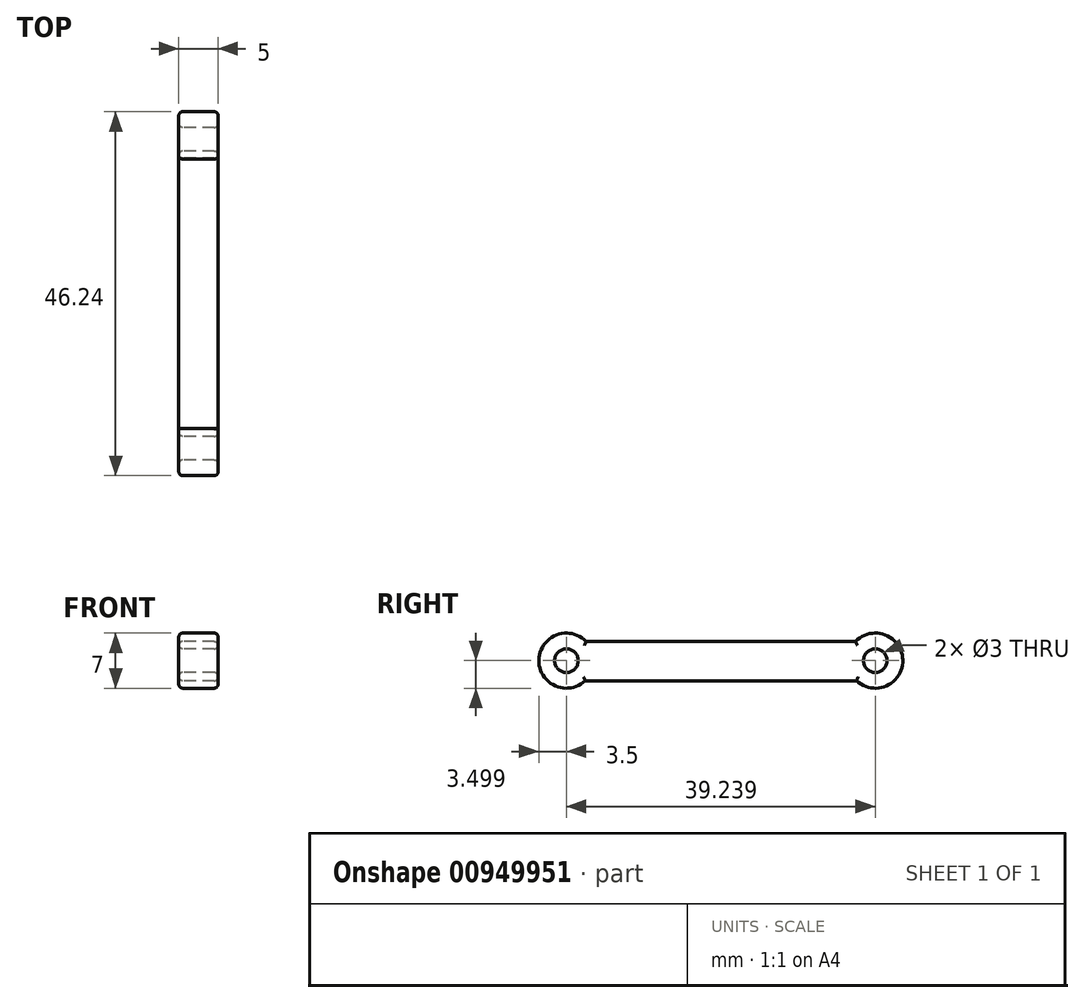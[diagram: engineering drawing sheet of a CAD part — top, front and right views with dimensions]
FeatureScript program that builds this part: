
annotation { "Feature Type Name" : "Feature", "Feature Type Description" : "" }
export const myFeature = defineFeature(function(context is Context, id is Id, definition is map)
    precondition{}
    {
        {
            var Q0;
            Q0=qCreatedBy(makeId("Right.planeOp"),FACE);
            var sketch = newSketch(context, id + "F0", { "sketchPlane" : qUnion([Q0])});
            skLineSegment(sketch, "E0", {"start": v(0, -22.45) * mm, "end": v(0, 65.15) * mm, "construction": true});
            skLineSegment(sketch, "E1", {"start": v(0, 65.15) * mm, "end": v(-56.9, 65.15) * mm, "construction": true});
            skCircle(sketch, "E2", {"center": v(-19.62, 65.15) * mm, "radius": 1.5 * mm});
            skCircle(sketch, "E3", {"center": v(-19.62, 65.15) * mm, "radius": 3.5 * mm});
            skLineSegment(sketch, "E4", {"start": v(-17.11, 67.59) * mm, "end": v(-12.11, 67.59) * mm});
            skLineSegment(sketch, "E5", {"start": v(-6.54, 62.59) * mm, "end": v(-22, 62.59) * mm});
            skLineSegment(sketch, "E6", {"start": v(-22, 62.59) * mm, "end": v(-17.11, 67.59) * mm});
            skLineSegment(sketch, "E7.MirrorCS", {"start": v(6.54, 62.59) * mm, "end": v(22, 62.59) * mm});
            skCircle(sketch, "E8.MirrorC", {"center": v(19.62, 65.15) * mm, "radius": 3.5 * mm});
            skLineSegment(sketch, "E9.MirrorCS", {"start": v(17.11, 67.59) * mm, "end": v(12.11, 67.59) * mm});
            skLineSegment(sketch, "E10.MirrorCS", {"start": v(22, 62.59) * mm, "end": v(17.11, 67.59) * mm});
            skLineSegment(sketch, "E11.MirrorCS", {"start": v(0, 65.15) * mm, "end": v(56.9, 65.15) * mm, "construction": true});
            skCircle(sketch, "E12.MirrorC", {"center": v(19.62, 65.15) * mm, "radius": 1.5 * mm});
            skLineSegment(sketch, "E13", {"start": v(-12.11, 67.59) * mm, "end": v(12.11, 67.59) * mm});
            skLineSegment(sketch, "E14", {"start": v(6.54, 62.59) * mm, "end": v(-6.54, 62.59) * mm});
            skSolve(sketch);
        }
        {
            var Q0;
            Q0 = qSketchRegion(id + "F0", true);
            extrude(context, id + "F1", {"entities" : qUnion([Q0]), "depth" : 5 * mm, "offsetDistance" : 25 * mm});
        }
        {
            var Q0;
            Q0=makeQuery(id+"F1.opExtrude","CAP_FACE",FACE,{"disambiguationData":[OSD([sQuery(id+"F0.wireOp",EDGE,"PsG27yTL-skAM-AQHq-AgSu-lJzymPvgla3L"),sQuery(id+"F0.wireOp",EDGE,"x8F9LROH-cmAM-jw7y-CWZf-tsfBcWcwgvpM"),sQuery(id+"F0.wireOp",EDGE,"E2"),sQuery(id+"F0.wireOp",EDGE,"E3"),sQuery(id+"F0.wireOp",EDGE,"B46dnGjq-MgKL-zzHq-BG8t-HNJFBw0L45we"),sQuery(id+"F0.wireOp",EDGE,"2Yd85arM-JVxp-JVfK-UykO-EWV6bo6VZNN6"),sQuery(id+"F0.wireOp",EDGE,"E4"),sQuery(id+"F0.wireOp",EDGE,"E5"),sQuery(id+"F0.wireOp",EDGE,"fPyJ3v05-W7tJ-lYo5-8Ni1-B8mxLdH9nyBu"),sQuery(id+"F0.wireOp",EDGE,"1A3QekKg-Qdfw-12Oe-YgYt-MgSBLqDep2W5")])],"isStart":false});
            var Q1;
            Q1=makeQuery(id+"F1.opExtrude","CAP_FACE",FACE,{"disambiguationData":[OSD([sQuery(id+"F0.wireOp",EDGE,"PsG27yTL-skAM-AQHq-AgSu-lJzymPvgla3L"),sQuery(id+"F0.wireOp",EDGE,"x8F9LROH-cmAM-jw7y-CWZf-tsfBcWcwgvpM"),sQuery(id+"F0.wireOp",EDGE,"E2"),sQuery(id+"F0.wireOp",EDGE,"E3"),sQuery(id+"F0.wireOp",EDGE,"B46dnGjq-MgKL-zzHq-BG8t-HNJFBw0L45we"),sQuery(id+"F0.wireOp",EDGE,"2Yd85arM-JVxp-JVfK-UykO-EWV6bo6VZNN6"),sQuery(id+"F0.wireOp",EDGE,"E4"),sQuery(id+"F0.wireOp",EDGE,"E5"),sQuery(id+"F0.wireOp",EDGE,"fPyJ3v05-W7tJ-lYo5-8Ni1-B8mxLdH9nyBu"),sQuery(id+"F0.wireOp",EDGE,"1A3QekKg-Qdfw-12Oe-YgYt-MgSBLqDep2W5")])],"isStart":true});
            fillet(context, id + "F2", {"entities" : qUnion([Q0, Q1]), "tangentPropagation" : true, "radius" : 0.5 * mm, "defaultsChanged" : true, "vertexSettings" : [], "allowEdgeOverflow" : false});
        }
    });
